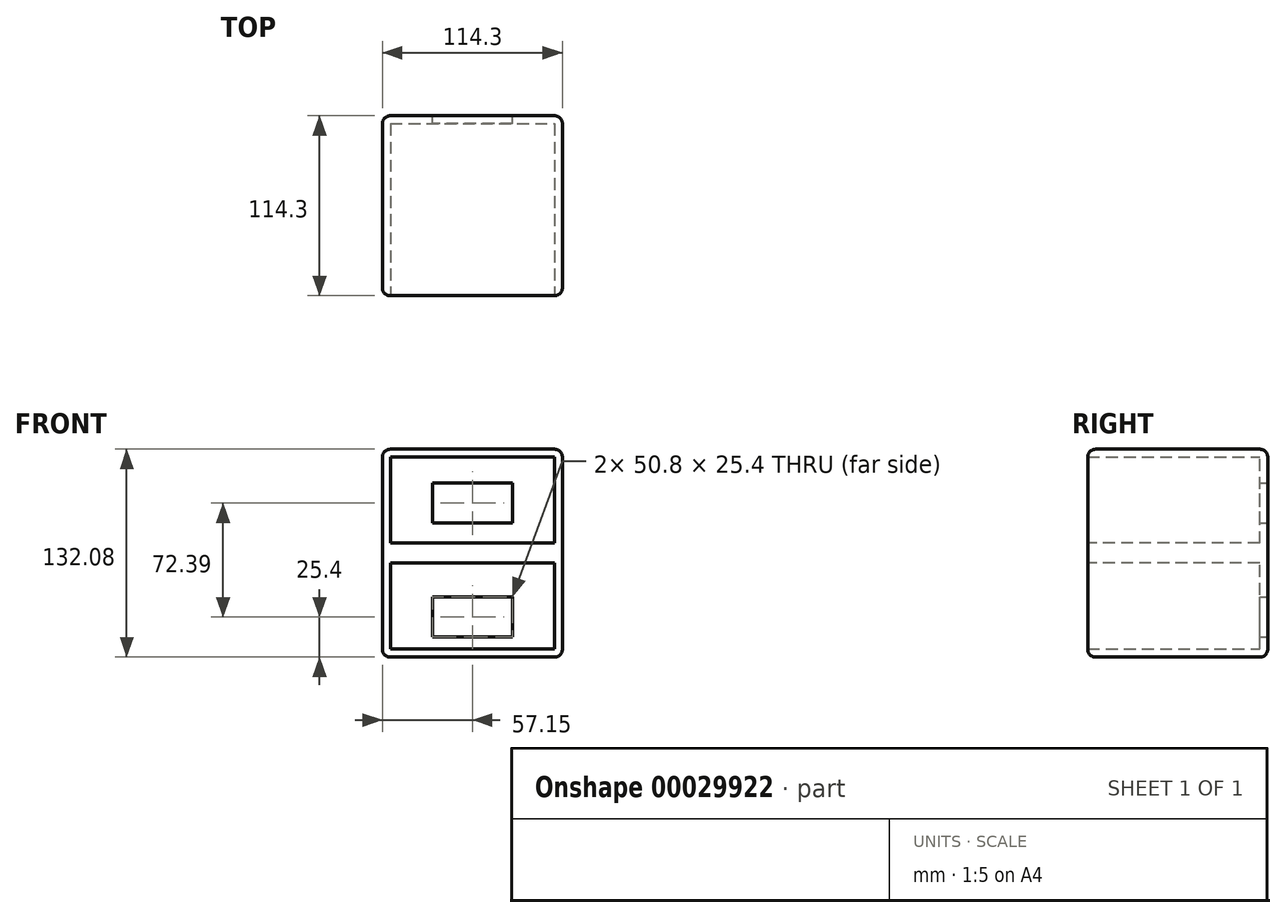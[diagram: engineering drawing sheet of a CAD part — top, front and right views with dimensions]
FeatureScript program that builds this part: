
annotation { "Feature Type Name" : "Feature", "Feature Type Description" : "" }
export const myFeature = defineFeature(function(context is Context, id is Id, definition is map)
    precondition{}
    {
        {
            var Q0;
            Q0=qCreatedBy(makeId("Front.planeOp"),FACE);
            var sketch = newSketch(context, id + "F0", { "sketchPlane" : qUnion([Q0])});
            skLineSegment(sketch, "E0.rect.bottom", {"start": v(57.15, -66.04) * mm, "end": v(-57.15, -66.04) * mm});
            skLineSegment(sketch, "E0.rect.top", {"start": v(57.15, 66.04) * mm, "end": v(-57.15, 66.04) * mm});
            skLineSegment(sketch, "E0.rect.left", {"start": v(57.15, -66.04) * mm, "end": v(57.15, 66.04) * mm});
            skLineSegment(sketch, "E0.rect.right", {"start": v(-57.15, -66.04) * mm, "end": v(-57.15, 66.04) * mm});
            skPoint(sketch, "E0.rect.middle", {"position": v(0, 0) * mm});
            skLineSegment(sketch, "E1.rect.bottom", {"start": v(57.15, -6.35) * mm, "end": v(-57.15, -6.35) * mm});
            skLineSegment(sketch, "E1.rect.top", {"start": v(57.15, 6.35) * mm, "end": v(-57.15, 6.35) * mm});
            skLineSegment(sketch, "E1.rect.left", {"start": v(57.15, -6.35) * mm, "end": v(57.15, 6.35) * mm});
            skLineSegment(sketch, "E1.rect.right", {"start": v(-57.15, -6.35) * mm, "end": v(-57.15, 6.35) * mm});
            skLineSegment(sketch, "E2.rect.bottom", {"start": v(25.4, -53.34) * mm, "end": v(-25.4, -53.34) * mm});
            skLineSegment(sketch, "E2.rect.top", {"start": v(25.4, -27.94) * mm, "end": v(-25.4, -27.94) * mm});
            skLineSegment(sketch, "E2.rect.left", {"start": v(25.4, -53.34) * mm, "end": v(25.4, -27.94) * mm});
            skLineSegment(sketch, "E2.rect.right", {"start": v(-25.4, -53.34) * mm, "end": v(-25.4, -27.94) * mm});
            skPoint(sketch, "E2.rect.middle", {"position": v(0, -40.64) * mm});
            skLineSegment(sketch, "E3.rect.bottom", {"start": v(25.4, 19.05) * mm, "end": v(-25.4, 19.05) * mm});
            skLineSegment(sketch, "E3.rect.top", {"start": v(25.4, 44.45) * mm, "end": v(-25.4, 44.45) * mm});
            skLineSegment(sketch, "E3.rect.left", {"start": v(25.4, 19.05) * mm, "end": v(25.4, 44.45) * mm});
            skLineSegment(sketch, "E3.rect.right", {"start": v(-25.4, 19.05) * mm, "end": v(-25.4, 44.45) * mm});
            skPoint(sketch, "E3.rect.middle", {"position": v(0, 31.75) * mm});
            skSolve(sketch);
        }
        {
            var Q0;
            Q0=qCreatedBy(makeId("Front.planeOp"),FACE);
            var sketch = newSketch(context, id + "F1", { "sketchPlane" : qUnion([Q0])});
            skLineSegment(sketch, "E4.0", {"start": v(-57.15, -66.04) * mm, "end": v(-57.15, 66.04) * mm});
            skLineSegment(sketch, "E4.1", {"start": v(57.15, 66.04) * mm, "end": v(-57.15, 66.04) * mm});
            skLineSegment(sketch, "E4.2", {"start": v(57.15, -66.04) * mm, "end": v(57.15, 66.04) * mm});
            skLineSegment(sketch, "E4.3", {"start": v(57.15, -66.04) * mm, "end": v(-57.15, -66.04) * mm});
            skSolve(sketch);
        }
        {
            var Q0;
            Q0 = qSketchRegion(id + "F1", true);
            extrude(context, id + "F2", {"entities" : qUnion([Q0]), "depth" : 114.3 * mm});
        }
        {
            var Q0;
            Q0=makeQuery(id+"F2.opExtrude","CAP_FACE",FACE,{"disambiguationData":[OSD([sQuery(id+"F1.wireOp",EDGE,"E4.0"),sQuery(id+"F1.wireOp",EDGE,"E4.1"),sQuery(id+"F1.wireOp",EDGE,"E4.2"),sQuery(id+"F1.wireOp",EDGE,"E4.3")])],"isStart":false});
            shell(context, id + "F3", {"entities" : qUnion([Q0]), "thickness" : 5.08 * mm});
        }
        {
            var Q0;
            Q0=qCreatedBy(makeId("Front.planeOp"),FACE);
            var sketch = newSketch(context, id + "F4", { "sketchPlane" : qUnion([Q0])});
            skLineSegment(sketch, "E5.0", {"start": v(57.15, 6.35) * mm, "end": v(-57.15, 6.35) * mm});
            skLineSegment(sketch, "E5.1", {"start": v(57.15, -6.35) * mm, "end": v(-57.15, -6.35) * mm});
            skLineSegment(sketch, "E5.2", {"start": v(-57.15, -6.35) * mm, "end": v(-57.15, 6.35) * mm});
            skLineSegment(sketch, "E5.3", {"start": v(57.15, -6.35) * mm, "end": v(57.15, 6.35) * mm});
            skSolve(sketch);
        }
        {
            var Q0;
            Q0 = qSketchRegion(id + "F4", true);
            var Q1;
            Q1=makeQuery(id+"F2.opExtrude","CAP_FACE",FACE,{"disambiguationData":[OSD([sQuery(id+"F1.wireOp",EDGE,"E4.0"),sQuery(id+"F1.wireOp",EDGE,"E4.1"),sQuery(id+"F1.wireOp",EDGE,"E4.2"),sQuery(id+"F1.wireOp",EDGE,"E4.3")])],"isStart":false});
            extrude(context, id + "F5", {"entities" : qUnion([Q0]), "operationType" : NewBodyOperationType.ADD, "endBound" : BoundingType.UP_TO_SURFACE, "endBoundEntityFace" : qUnion([Q1]), "depth" : 25 * mm});
        }
        {
            var Q0;
            Q0=qCreatedBy(makeId("Front.planeOp"),FACE);
            var sketch = newSketch(context, id + "F6", { "sketchPlane" : qUnion([Q0])});
            skLineSegment(sketch, "E6.0", {"start": v(25.4, 19.05) * mm, "end": v(-25.4, 19.05) * mm});
            skLineSegment(sketch, "E6.1", {"start": v(-25.4, 19.05) * mm, "end": v(-25.4, 44.45) * mm});
            skLineSegment(sketch, "E6.2", {"start": v(25.4, 44.45) * mm, "end": v(-25.4, 44.45) * mm});
            skLineSegment(sketch, "E6.3", {"start": v(25.4, 19.05) * mm, "end": v(25.4, 44.45) * mm});
            skLineSegment(sketch, "E6.4", {"start": v(25.4, -27.94) * mm, "end": v(-25.4, -27.94) * mm});
            skLineSegment(sketch, "E6.5", {"start": v(25.4, -53.34) * mm, "end": v(25.4, -27.94) * mm});
            skLineSegment(sketch, "E6.6", {"start": v(25.4, -53.34) * mm, "end": v(-25.4, -53.34) * mm});
            skLineSegment(sketch, "E6.7", {"start": v(-25.4, -53.34) * mm, "end": v(-25.4, -27.94) * mm});
            skSolve(sketch);
        }
        {
            var Q0;
            Q0 = qSketchRegion(id + "F6", true);
            extrude(context, id + "F7", {"entities" : qUnion([Q0]), "operationType" : NewBodyOperationType.REMOVE, "endBound" : BoundingType.UP_TO_NEXT, "depth" : 25 * mm});
        }
        {
            var Q0;
            Q0=makeQuery(id+"F2.opExtrude","SWEPT_EDGE",EDGE,{"disambiguationData":[OSD([sQuery(id+"F1.wireOp",EDGE,"E4.1"),sQuery(id+"F1.wireOp",EDGE,"E4.2")])]});
            var Q1;
            Q1=makeQuery(id+"F2.opExtrude","SWEPT_EDGE",EDGE,{"disambiguationData":[OSD([sQuery(id+"F1.wireOp",EDGE,"E4.0"),sQuery(id+"F1.wireOp",EDGE,"E4.1")])]});
            var Q2;
            Q2=makeQuery(id+"F2.opExtrude","CAP_EDGE",EDGE,{"disambiguationData":[OSD([sQuery(id+"F1.wireOp",EDGE,"E4.0")])],"isStart":false});
            var Q3;
            Q3=makeQuery(id+"F2.opExtrude","CAP_EDGE",EDGE,{"disambiguationData":[OSD([sQuery(id+"F1.wireOp",EDGE,"E4.2")])],"isStart":false});
            var Q4;
            Q4=makeQuery(id+"F2.opExtrude","CAP_EDGE",EDGE,{"disambiguationData":[OSD([sQuery(id+"F1.wireOp",EDGE,"E4.1")])],"isStart":false});
            var Q5;
            Q5=makeQuery(id+"F2.opExtrude","CAP_EDGE",EDGE,{"disambiguationData":[OSD([sQuery(id+"F1.wireOp",EDGE,"E4.2")])],"isStart":true});
            var Q6;
            Q6=makeQuery(id+"F2.opExtrude","SWEPT_EDGE",EDGE,{"disambiguationData":[OSD([sQuery(id+"F1.wireOp",EDGE,"E4.2"),sQuery(id+"F1.wireOp",EDGE,"E4.3")])]});
            var Q7;
            Q7=makeQuery(id+"F2.opExtrude","CAP_EDGE",EDGE,{"disambiguationData":[OSD([sQuery(id+"F1.wireOp",EDGE,"E4.3")])],"isStart":false});
            var Q8;
            Q8=makeQuery(id+"F2.opExtrude","SWEPT_EDGE",EDGE,{"disambiguationData":[OSD([sQuery(id+"F1.wireOp",EDGE,"E4.0"),sQuery(id+"F1.wireOp",EDGE,"E4.3")])]});
            var Q9;
            Q9=makeQuery(id+"F2.opExtrude","CAP_EDGE",EDGE,{"disambiguationData":[OSD([sQuery(id+"F1.wireOp",EDGE,"E4.3")])],"isStart":true});
            var Q10;
            Q10=makeQuery(id+"F2.opExtrude","CAP_EDGE",EDGE,{"disambiguationData":[OSD([sQuery(id+"F1.wireOp",EDGE,"E4.1")])],"isStart":true});
            var Q11;
            Q11=makeQuery(id+"F2.opExtrude","CAP_EDGE",EDGE,{"disambiguationData":[OSD([sQuery(id+"F1.wireOp",EDGE,"E4.0")])],"isStart":true});
            fillet(context, id + "F8", {"entities" : qUnion([Q0, Q1, Q2, Q3, Q4, Q5, Q6, Q7, Q8, Q9, Q10, Q11]), "radius" : 5 * mm, "tangentPropagation" : true, "allowEdgeOverflow" : false});
        }
    });
